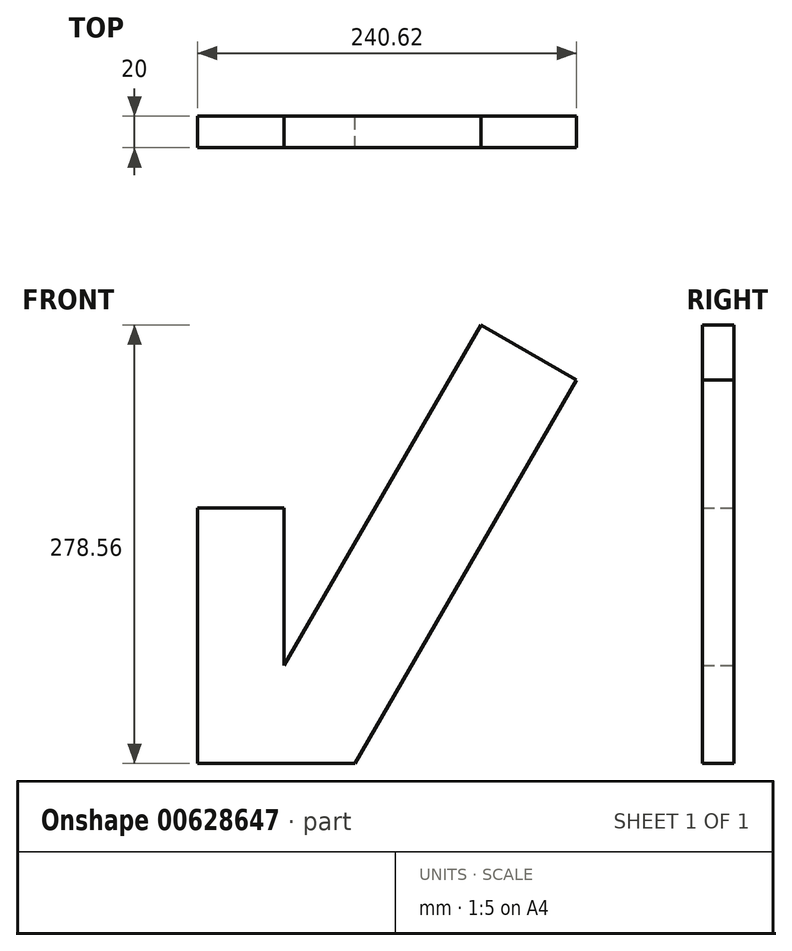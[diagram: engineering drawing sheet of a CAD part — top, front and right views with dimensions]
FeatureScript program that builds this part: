
annotation { "Feature Type Name" : "Feature", "Feature Type Description" : "" }
export const myFeature = defineFeature(function(context is Context, id is Id, definition is map)
    precondition{}
    {
        {
            var Q0;
            Q0=qCreatedBy(makeId("Front.planeOp"),FACE);
            var sketch = newSketch(context, id + "F0", { "sketchPlane" : qUnion([Q0])});
            skLineSegment(sketch, "E0", {"start": v(0, 0) * mm, "end": v(100, 0) * mm});
            skLineSegment(sketch, "E1", {"start": v(100, 0) * mm, "end": v(240.62, 243.56) * mm});
            skLineSegment(sketch, "E2", {"start": v(240.62, 243.56) * mm, "end": v(180, 278.56) * mm});
            skLineSegment(sketch, "E3", {"start": v(180, 278.56) * mm, "end": v(55, 62.06) * mm});
            skLineSegment(sketch, "E4", {"start": v(55, 62.06) * mm, "end": v(55, 162.06) * mm});
            skLineSegment(sketch, "E5", {"start": v(55, 162.06) * mm, "end": v(0, 162.06) * mm});
            skLineSegment(sketch, "E6", {"start": v(0, 162.06) * mm, "end": v(0, 0) * mm});
            skSolve(sketch);
        }
        {
            var Q0;
            Q0 = qSketchRegion(id + "F0", true);
            extrude(context, id + "F1", {"entities" : qUnion([Q0]), "depth" : 20 * mm, "offsetDistance" : 25 * mm});
        }
    });
